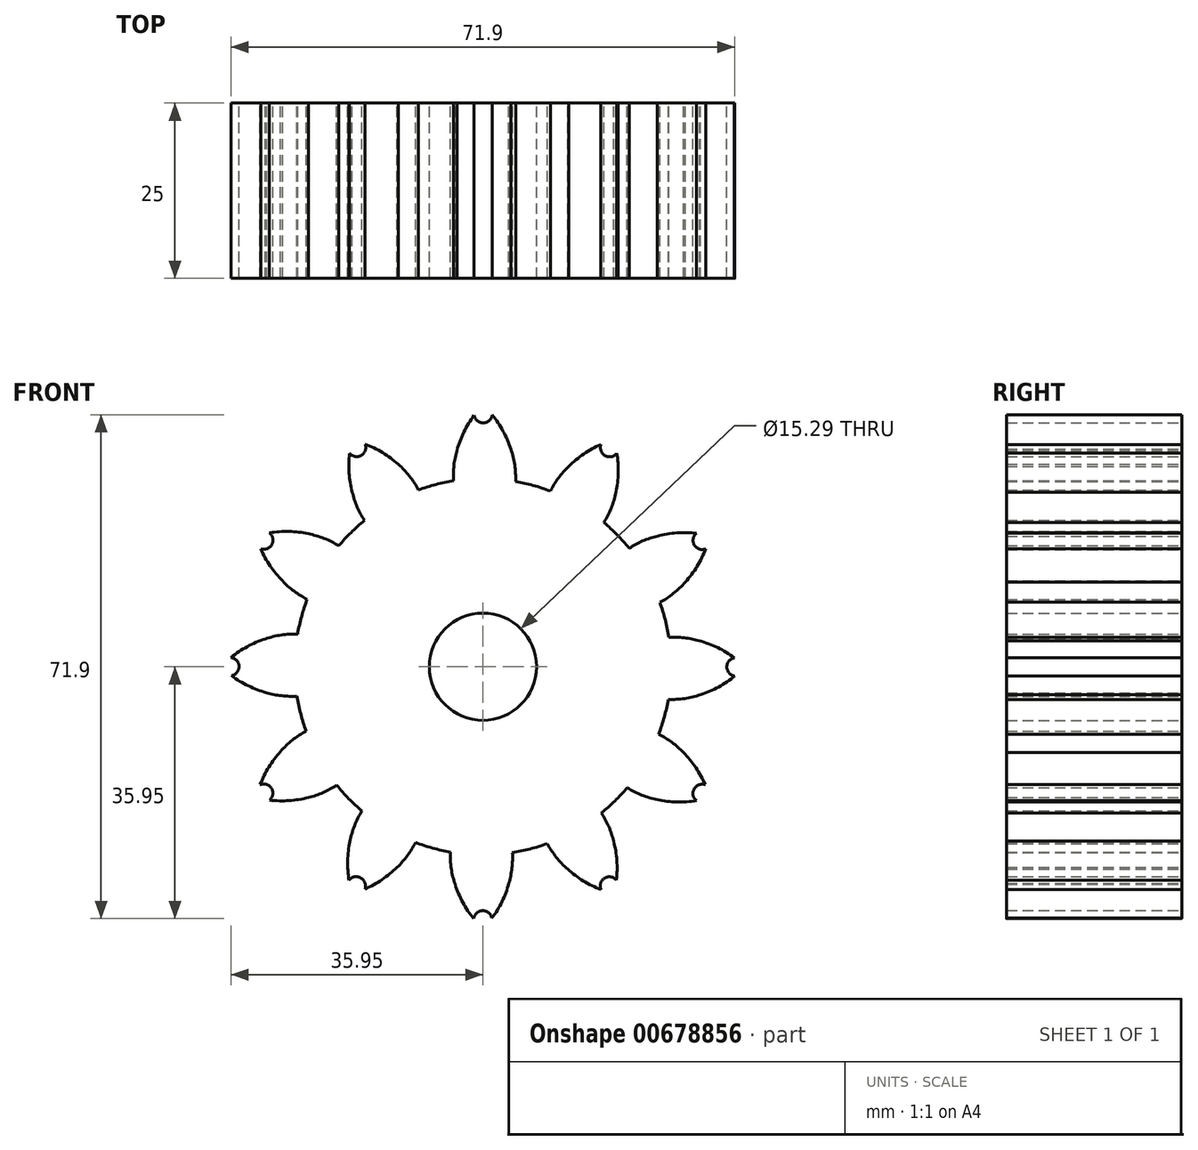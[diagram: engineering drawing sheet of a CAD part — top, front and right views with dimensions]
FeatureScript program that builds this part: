
annotation { "Feature Type Name" : "Feature", "Feature Type Description" : "" }
export const myFeature = defineFeature(function(context is Context, id is Id, definition is map)
    precondition{}
    {
        {
            var Q0;
            Q0=qCreatedBy(makeId("Front.planeOp"),FACE);
            var sketch = newSketch(context, id + "F0", { "sketchPlane" : qUnion([Q0])});
            skCircle(sketch, "E0", {"center": v(0, 0) * mm, "radius": 26.86 * mm});
            skCircle(sketch, "E1", {"center": v(0, 0) * mm, "radius": 29.34 * mm, "construction": true});
            skCircle(sketch, "E2", {"center": v(0, 0) * mm, "radius": 31.75 * mm, "construction": true});
            skLineSegment(sketch, "E3", {"start": v(0, 0) * mm, "end": v(0, 97.8) * mm, "construction": true});
            skLineSegment(sketch, "E4", {"start": v(0, 0) * mm, "end": v(-6.4, 97.8) * mm, "construction": true});
            skLineSegment(sketch, "E5", {"start": v(0, 29.34) * mm, "end": v(-71.5, 29.34) * mm, "construction": true});
            skLineSegment(sketch, "E6", {"start": v(0, 29.34) * mm, "end": v(-73, 2.77) * mm, "construction": true});
            skCircle(sketch, "E7", {"center": v(0, 0) * mm, "radius": 27.57 * mm, "construction": true});
            skCircle(sketch, "E8", {"center": v(0, 29.34) * mm, "radius": 14.6 * mm, "construction": true});
            skCircle(sketch, "E9", {"center": v(-13.72, 24.34) * mm, "radius": 14.6 * mm, "construction": true});
            skPoint(sketch, "E10.0.midPoint", {"position": v(11.93, -17.39) * mm});
            skArc(sketch, "E11", {"start": v(3.97, 31.07) * mm, "mid": v(2.88, 33.63) * mm, "end": v(1.32, 35.95) * mm});
            skArc(sketch, "E12", {"start": v(4.64, 26.07) * mm, "mid": v(4.56, 28.6) * mm, "end": v(3.97, 31.07) * mm});
            skArc(sketch, "E13.MirrorCS", {"start": v(-3.7, 30.9) * mm, "mid": v(-2.72, 33.5) * mm, "end": v(-1.27, 35.89) * mm});
            skArc(sketch, "E14.MirrorCS", {"start": v(-4.14, 25.88) * mm, "mid": v(-4.17, 28.4) * mm, "end": v(-3.7, 30.9) * mm});
            skArc(sketch, "E15", {"start": v(-1.27, 35.89) * mm, "mid": v(0.05, 34.8) * mm, "end": v(1.32, 35.95) * mm});
            skCircle(sketch, "E16", {"center": v(0, 0) * mm, "radius": 7.65 * mm});
            skSolve(sketch);
        }
        {
            var Q0;
            {var subQ2=sQuery(id+"F0.wireOp",EDGE,"E11");Q0=makeQuery(id+"F0.imprint","IMPRINT",FACE,{"disambiguationData":[TD([[makeQuery(id+"F0.imprint","IMPRINT",EDGE,{"derivedFrom":subQ2}),1.0]])]});}
            var Q1;
            {var subQ0=sQuery(id+"F0.wireOp",EDGE,"E0");var subQ1=makeQuery(id+"F0.imprint","INTERSECT",VERTEX,{"derivedFrom":[subQ0,sQuery(id+"F0.wireOp",EDGE,"E12")]});Q1=makeQuery(id+"F0.imprint","IMPRINT",FACE,{"disambiguationData":[TD([[makeQuery(id+"F0.imprint","IMPRINT",EDGE,{"disambiguationData":[TD([[subQ1,-1.0]])],"derivedFrom":subQ0}),1.0]])]});}
            extrude(context, id + "F1", {"entities" : qUnion([Q0, Q1]), "depth" : 25 * mm, "offsetDistance" : 25 * mm});
        }
        {
            var Q0;
            Q0=makeQuery(id+"F1.opExtrude","SWEPT_BODY",BODY,{"disambiguationData":[OSD([sQuery(id+"F0.wireOp",EDGE,"E0"),sQuery(id+"F0.wireOp",EDGE,"E11"),sQuery(id+"F0.wireOp",EDGE,"E12"),sQuery(id+"F0.wireOp",EDGE,"E13.MirrorCS"),sQuery(id+"F0.wireOp",EDGE,"E14.MirrorCS"),sQuery(id+"F0.wireOp",EDGE,"E15")])]});
            var Q1;
            Q1=makeQuery(id+"F1.opExtrude","SWEPT_FACE",FACE,{"disambiguationData":[OSD([sQuery(id+"F0.wireOp",EDGE,"E0")])]});
            circularPattern(context, id + "F2", {"operationType" : NewBodyOperationType.ADD, "entities" : qUnion([Q0]), "axis" : qUnion([Q1]), "angle" : 360 * degree, "instanceCount" : 12, "equalSpace" : true});
        }
    });
